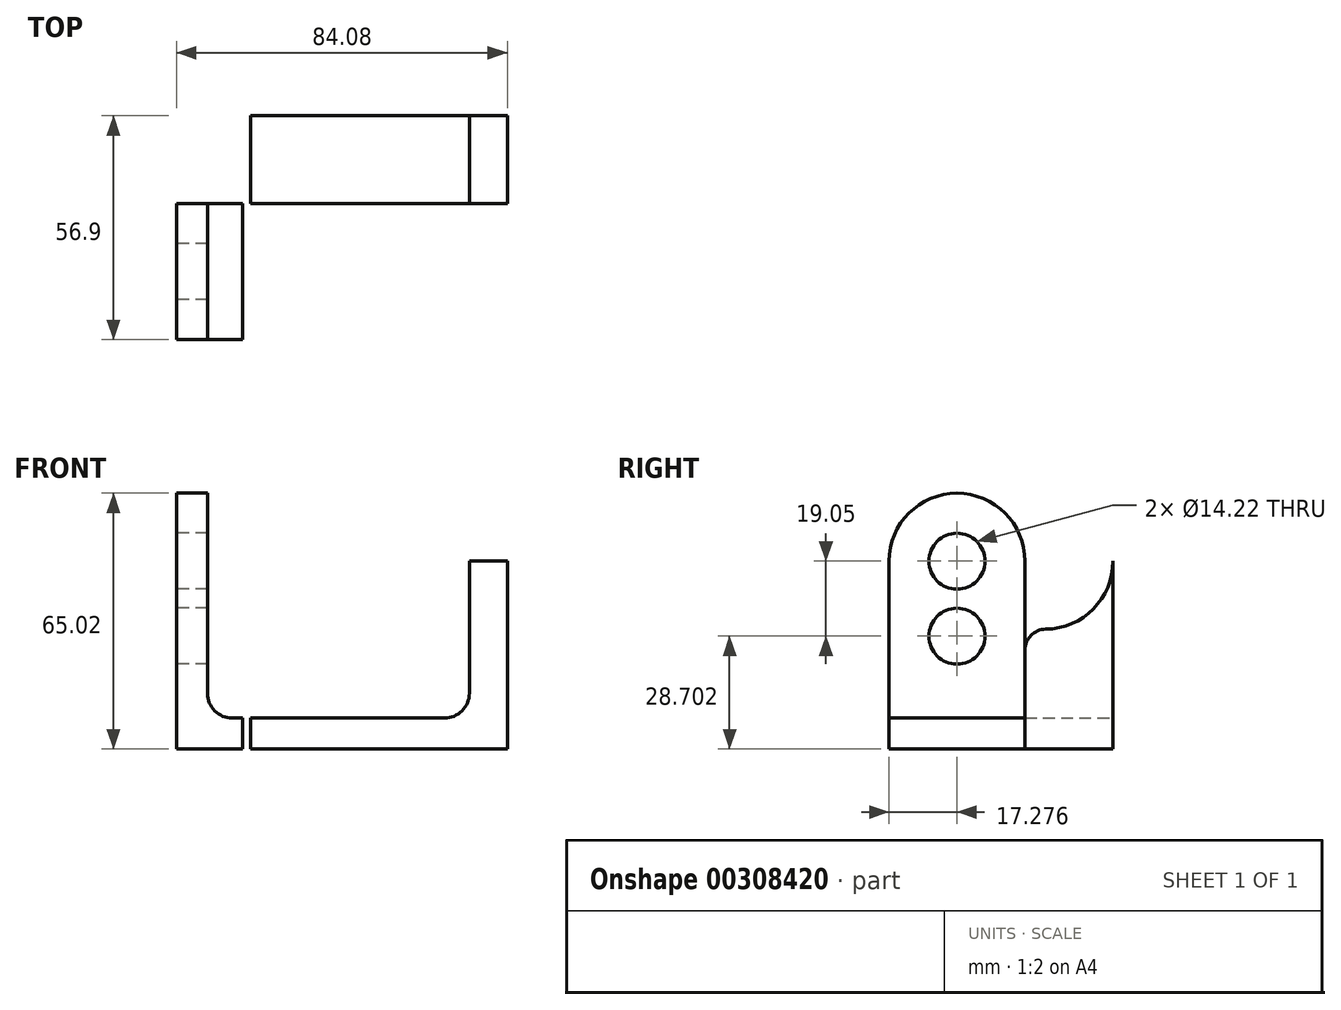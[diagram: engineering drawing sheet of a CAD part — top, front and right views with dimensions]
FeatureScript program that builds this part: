
annotation { "Feature Type Name" : "Feature", "Feature Type Description" : "" }
export const myFeature = defineFeature(function(context is Context, id is Id, definition is map)
    precondition{}
    {
        {
            var Q0;
            Q0=qCreatedBy(makeId("Front.planeOp"),FACE);
            var sketch = newSketch(context, id + "F0", { "sketchPlane" : qUnion([Q0])});
            skLineSegment(sketch, "E0", {"start": v(-42.04, 0) * mm, "end": v(42.04, 0) * mm});
            skLineSegment(sketch, "E1", {"start": v(42.04, 0) * mm, "end": v(42.04, 65.02) * mm});
            skLineSegment(sketch, "E2", {"start": v(42.04, 65.02) * mm, "end": v(32.38, 65.02) * mm});
            skLineSegment(sketch, "E3", {"start": v(32.39, 65.02) * mm, "end": v(32.39, 14.22) * mm});
            skLineSegment(sketch, "E4", {"start": v(26.04, 7.87) * mm, "end": v(-27.81, 7.87) * mm});
            skLineSegment(sketch, "E5", {"start": v(-34.16, 14.22) * mm, "end": v(-34.16, 65.02) * mm});
            skLineSegment(sketch, "E6", {"start": v(-34.16, 65.02) * mm, "end": v(-42.04, 65.02) * mm});
            skLineSegment(sketch, "E7", {"start": v(-42.04, 65.02) * mm, "end": v(-42.04, 0) * mm});
            skPoint(sketch, "E8.visualSharp", {"position": v(-34.16, 7.87) * mm});
            skArc(sketch, "E8.filletArc", {"start": v(-34.16, 14.22) * mm, "mid": v(-32.3, 9.73) * mm, "end": v(-27.81, 7.87) * mm});
            skPoint(sketch, "E9.visualSharp", {"position": v(32.39, 7.87) * mm});
            skArc(sketch, "E9.filletArc", {"start": v(26.04, 7.87) * mm, "mid": v(30.53, 9.73) * mm, "end": v(32.39, 14.22) * mm});
            skSolve(sketch);
        }
        {
            var Q0;
            Q0 = qSketchRegion(id + "F0", true);
            extrude(context, id + "F1", {"entities" : qUnion([Q0]), "depth" : 79.25 * mm});
        }
        {
            var Q0;
            Q0=makeQuery(id+"F1.opExtrude","SWEPT_FACE",FACE,{"disambiguationData":[OSD([sQuery(id+"F0.wireOp",EDGE,"E1")])]});
            var sketch = newSketch(context, id + "F2", { "sketchPlane" : qUnion([Q0])});
            skArc(sketch, "E10", {"start": v(-61.98, 65.02) * mm, "mid": v(-79.25, 47.85) * mm, "end": v(-62.17, 30.48) * mm});
            skLineSegment(sketch, "E11", {"start": v(-61.98, 65.02) * mm, "end": v(-39.62, 65.02) * mm});
            skLineSegment(sketch, "E12", {"start": v(-56.9, 0) * mm, "end": v(-56.9, 25.15) * mm});
            skLineSegment(sketch, "E13", {"start": v(-56.9, 0) * mm, "end": v(-39.62, 0) * mm});
            skLineSegment(sketch, "E14", {"start": v(-62.17, 30.48) * mm, "end": v(-62.17, 30.48) * mm});
            skPoint(sketch, "E15.center.orphan", {"position": v(-39.62, 47.75) * mm});
            skPoint(sketch, "E16.visualSharp", {"position": v(-56.9, 30.42) * mm});
            skArc(sketch, "E16.filletArc", {"start": v(-56.9, 25.15) * mm, "mid": v(-58.44, 28.9) * mm, "end": v(-62.17, 30.48) * mm});
            skPoint(sketch, "E17.visualSharp", {"position": v(-22.55, 30.04) * mm});
            skArc(sketch, "E18", {"start": v(-61.98, 54.86) * mm, "mid": v(-69.09, 47.75) * mm, "end": v(-61.98, 40.64) * mm});
            skLineSegment(sketch, "E19", {"start": v(-61.98, 54.86) * mm, "end": v(-39.62, 54.86) * mm});
            skLineSegment(sketch, "E20", {"start": v(-61.98, 40.64) * mm, "end": v(-39.62, 40.64) * mm});
            skLineSegment(sketch, "E21", {"start": v(-39.62, 62.85) * mm, "end": v(-39.62, -10.25) * mm, "construction": true});
            skPoint(sketch, "E22.center.orphan", {"position": v(-17.27, 47.75) * mm});
            skPoint(sketch, "E23.orphan", {"position": v(-22.35, 0) * mm});
            skLineSegment(sketch, "E24.MirrorCS", {"start": v(-17.27, 65.02) * mm, "end": v(-39.62, 65.02) * mm});
            skArc(sketch, "E25.MirrorCS", {"start": v(-17.27, 65.02) * mm, "mid": v(0, 47.85) * mm, "end": v(-17.08, 30.48) * mm});
            skArc(sketch, "E26.MirrorCS", {"start": v(-17.27, 54.86) * mm, "mid": v(-10.16, 47.75) * mm, "end": v(-17.27, 40.64) * mm});
            skLineSegment(sketch, "E27.MirrorCS", {"start": v(-17.27, 54.86) * mm, "end": v(-39.62, 54.86) * mm});
            skLineSegment(sketch, "E28.MirrorCS", {"start": v(-17.27, 40.64) * mm, "end": v(-39.62, 40.64) * mm});
            skArc(sketch, "E29.MirrorCS", {"start": v(-22.35, 25.15) * mm, "mid": v(-20.81, 28.9) * mm, "end": v(-17.08, 30.48) * mm});
            skLineSegment(sketch, "E30.MirrorCS", {"start": v(-22.35, 0) * mm, "end": v(-22.35, 25.15) * mm});
            skLineSegment(sketch, "E31.MirrorCS", {"start": v(-22.35, 0) * mm, "end": v(-39.62, 0) * mm});
            skSolve(sketch);
        }
        {
            var Q0;
            {var subQ4=sQuery(id+"F2.wireOp",EDGE,"E12");Q0=makeQuery(id+"F2.imprint","IMPRINT",FACE,{"disambiguationData":[TD([[makeQuery(id+"F2.imprint","IMPRINT",EDGE,{"derivedFrom":subQ4}),1.0]])]});}
            var Q1;
            Q1=makeQuery(id+"F2.imprint","IMPRINT",FACE,{"disambiguationData":[TD([[makeQuery(id+"F2.imprint","IMPRINT",EDGE,{"derivedFrom":sQuery(id+"F2.wireOp",EDGE,"E18")}),1.0]])]});
            var Q2;
            {var subQ5=sQuery(id+"F2.wireOp",EDGE,"E29.MirrorCS");Q2=makeQuery(id+"F2.imprint","IMPRINT",FACE,{"disambiguationData":[TD([[makeQuery(id+"F2.imprint","IMPRINT",EDGE,{"derivedFrom":subQ5}),-1.0]])]});}
            var Q3;
            {var subQ0=sQuery(id+"F2.wireOp",EDGE,"E25.MirrorCS");var subQ1=sQuery(id+"F0.wireOp",EDGE,"E1");var subQ4=makeQuery(id+"F1.opExtrude","CAP_EDGE",EDGE,{"disambiguationData":[OSD([subQ1])],"isStart":true});var subQ5=makeQuery(id+"F2.imprint","INTERSECT",VERTEX,{"derivedFrom":[subQ4,subQ0]});Q3=makeQuery(id+"F2.imprint","IMPRINT",FACE,{"disambiguationData":[TD([[makeQuery(id+"F2.imprint","IMPRINT",EDGE,{"disambiguationData":[TD([[subQ5,-1.0]])],"derivedFrom":subQ4}),1.0]])]});}
            var Q4;
            {var subQ0=sQuery(id+"F2.wireOp",EDGE,"E10");var subQ1=sQuery(id+"F0.wireOp",EDGE,"E1");var subQ4=makeQuery(id+"F1.opExtrude","CAP_EDGE",EDGE,{"disambiguationData":[OSD([subQ1])],"isStart":false});var subQ5=makeQuery(id+"F2.imprint","INTERSECT",VERTEX,{"derivedFrom":[subQ4,subQ0]});Q4=makeQuery(id+"F2.imprint","IMPRINT",FACE,{"disambiguationData":[TD([[makeQuery(id+"F2.imprint","IMPRINT",EDGE,{"disambiguationData":[TD([[subQ5,-1.0]])],"derivedFrom":subQ4}),-1.0]])]});}
            extrude(context, id + "F3", {"entities" : qUnion([Q0, Q1, Q2, Q3, Q4]), "operationType" : NewBodyOperationType.REMOVE, "oppositeDirection" : true, "depth" : 67.3 * mm});
        }
        {
            var Q0;
            Q0=makeQuery(id+"F1.opExtrude","SWEPT_FACE",FACE,{"disambiguationData":[OSD([sQuery(id+"F0.wireOp",EDGE,"E7")])]});
            var sketch = newSketch(context, id + "F4", { "sketchPlane" : qUnion([Q0])});
            skArc(sketch, "E32", {"start": v(56.9, 47.75) * mm, "mid": v(39.62, 65.02) * mm, "end": v(22.35, 47.75) * mm});
            skLineSegment(sketch, "E33", {"start": v(22.35, 47.75) * mm, "end": v(22.35, 0) * mm});
            skLineSegment(sketch, "E34", {"start": v(22.35, 0) * mm, "end": v(56.9, 0) * mm});
            skLineSegment(sketch, "E35", {"start": v(56.9, 0) * mm, "end": v(56.9, 47.75) * mm});
            skCircle(sketch, "E36", {"center": v(39.62, 47.75) * mm, "radius": 7.11 * mm});
            skCircle(sketch, "E37", {"center": v(39.62, 28.7) * mm, "radius": 7.11 * mm});
            skSolve(sketch);
        }
        {
            var Q0;
            {var subQ3=sQuery(id+"F4.wireOp",EDGE,"E33");Q0=makeQuery(id+"F4.imprint","IMPRINT",FACE,{"disambiguationData":[TD([[makeQuery(id+"F4.imprint","IMPRINT",EDGE,{"derivedFrom":subQ3}),-1.0]])]});}
            var Q1;
            {var subQ2=sQuery(id+"F4.wireOp",EDGE,"E35");Q1=makeQuery(id+"F4.imprint","IMPRINT",FACE,{"disambiguationData":[TD([[makeQuery(id+"F4.imprint","IMPRINT",EDGE,{"derivedFrom":subQ2}),-1.0]])]});}
            var Q2;
            Q2=makeQuery(id+"F4.imprint","IMPRINT",FACE,{"disambiguationData":[TD([[makeQuery(id+"F4.imprint","IMPRINT",EDGE,{"derivedFrom":sQuery(id+"F4.wireOp",EDGE,"E36")}),1.0]])]});
            var Q3;
            Q3=makeQuery(id+"F4.imprint","IMPRINT",FACE,{"disambiguationData":[TD([[makeQuery(id+"F4.imprint","IMPRINT",EDGE,{"derivedFrom":sQuery(id+"F4.wireOp",EDGE,"E37")}),1.0]])]});
            var Q4;
            Q4=makeQuery(id+"F1.opExtrude","SWEPT_FACE",FACE,{"disambiguationData":[OSD([sQuery(id+"F0.wireOp",EDGE,"E1")])]});
            extrude(context, id + "F5", {"entities" : qUnion([Q0, Q1, Q2, Q3, Q4]), "operationType" : NewBodyOperationType.REMOVE, "oppositeDirection" : true, "depth" : 18.8 * mm});
        }
    });
